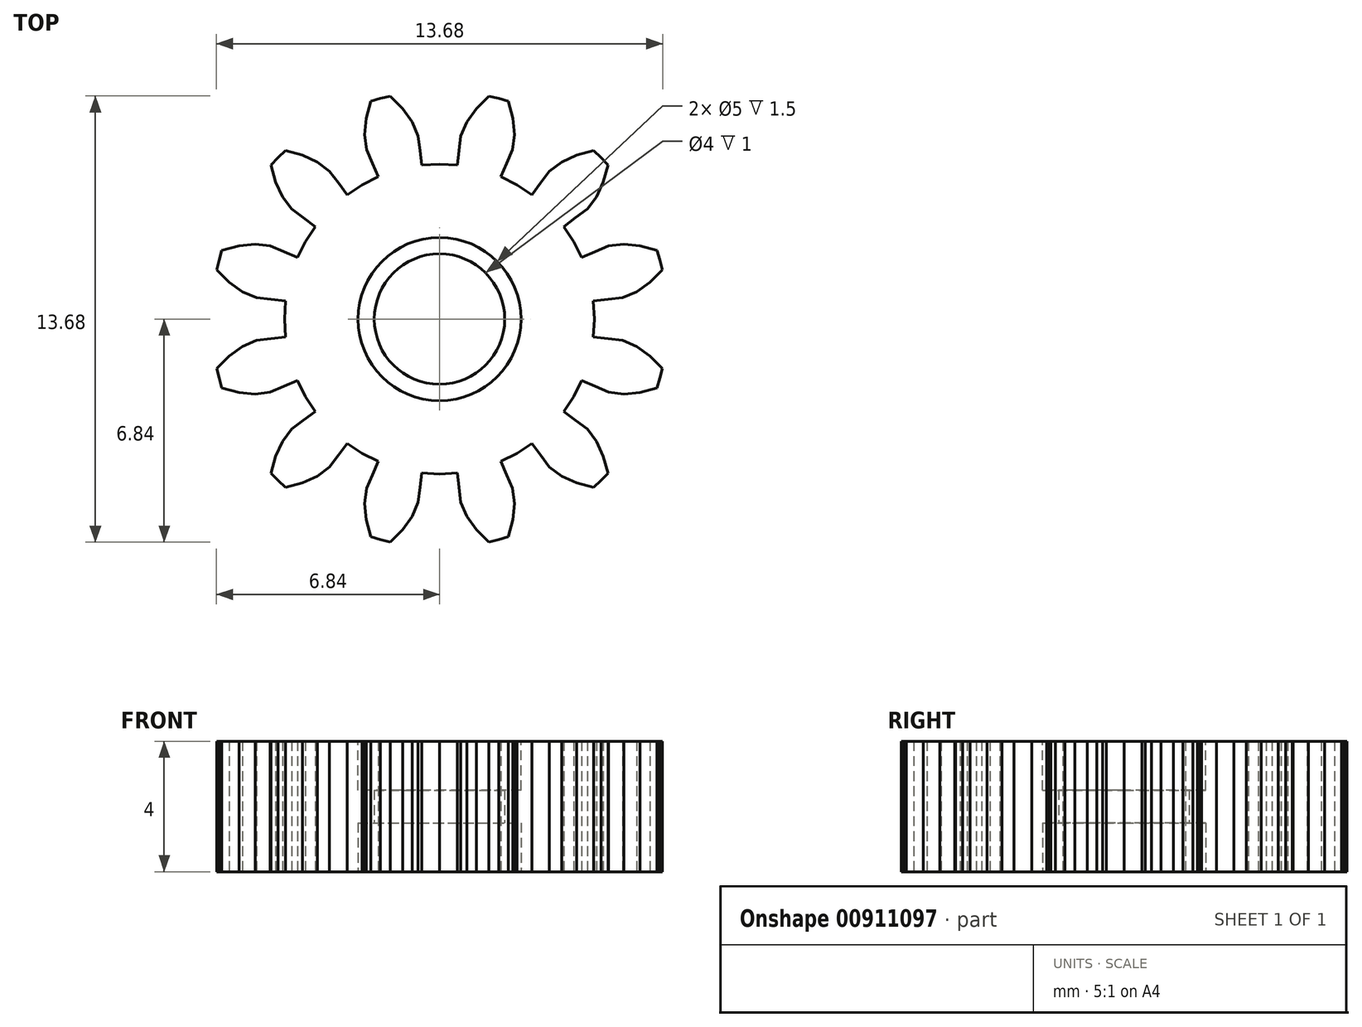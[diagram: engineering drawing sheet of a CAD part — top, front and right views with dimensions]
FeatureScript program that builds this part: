
annotation { "Feature Type Name" : "Feature", "Feature Type Description" : "" }
export const myFeature = defineFeature(function(context is Context, id is Id, definition is map)
    precondition{}
    {
        {
            var Q0;
            Q0=qCreatedBy(makeId("Top.planeOp"),FACE);
            var sketch = newSketch(context, id + "F0", { "sketchPlane" : qUnion([Q0])});
            skLineSegment(sketch, "E0", {"start": v(4.75, 0) * mm, "end": v(4.72, 0.55) * mm});
            skLineSegment(sketch, "E1", {"start": v(4.72, 0.55) * mm, "end": v(5.17, 0.6) * mm});
            skLineSegment(sketch, "E2", {"start": v(5.17, 0.6) * mm, "end": v(5.61, 0.65) * mm});
            skLineSegment(sketch, "E3", {"start": v(5.61, 0.65) * mm, "end": v(6.04, 0.84) * mm});
            skLineSegment(sketch, "E4", {"start": v(6.04, 0.84) * mm, "end": v(6.45, 1.13) * mm});
            skLineSegment(sketch, "E5", {"start": v(6.45, 1.13) * mm, "end": v(6.84, 1.51) * mm});
            skLineSegment(sketch, "E6", {"start": v(6.84, 1.51) * mm, "end": v(6.76, 1.81) * mm});
            skLineSegment(sketch, "E7", {"start": v(6.76, 1.81) * mm, "end": v(6.67, 2.1) * mm});
            skLineSegment(sketch, "E8", {"start": v(6.67, 2.1) * mm, "end": v(6.15, 2.25) * mm});
            skLineSegment(sketch, "E9", {"start": v(6.15, 2.25) * mm, "end": v(5.65, 2.3) * mm});
            skLineSegment(sketch, "E10", {"start": v(5.65, 2.3) * mm, "end": v(5.19, 2.24) * mm});
            skLineSegment(sketch, "E11", {"start": v(5.19, 2.24) * mm, "end": v(4.77, 2.06) * mm});
            skLineSegment(sketch, "E12", {"start": v(4.77, 2.06) * mm, "end": v(4.36, 1.88) * mm});
            skLineSegment(sketch, "E13", {"start": v(4.36, 1.88) * mm, "end": v(4.11, 2.38) * mm});
            skLineSegment(sketch, "E14", {"start": v(4.11, 2.38) * mm, "end": v(3.81, 2.84) * mm});
            skLineSegment(sketch, "E15", {"start": v(3.81, 2.84) * mm, "end": v(4.17, 3.1) * mm});
            skLineSegment(sketch, "E16", {"start": v(4.17, 3.1) * mm, "end": v(4.53, 3.37) * mm});
            skLineSegment(sketch, "E17", {"start": v(4.53, 3.37) * mm, "end": v(4.82, 3.74) * mm});
            skLineSegment(sketch, "E18", {"start": v(4.82, 3.74) * mm, "end": v(5.02, 4.2) * mm});
            skLineSegment(sketch, "E19", {"start": v(5.02, 4.2) * mm, "end": v(5.16, 4.73) * mm});
            skLineSegment(sketch, "E20", {"start": v(5.16, 4.73) * mm, "end": v(4.95, 4.95) * mm});
            skLineSegment(sketch, "E21", {"start": v(4.95, 4.95) * mm, "end": v(4.73, 5.16) * mm});
            skLineSegment(sketch, "E22", {"start": v(4.73, 5.16) * mm, "end": v(4.2, 5.02) * mm});
            skLineSegment(sketch, "E23", {"start": v(4.2, 5.02) * mm, "end": v(3.74, 4.82) * mm});
            skLineSegment(sketch, "E24", {"start": v(3.74, 4.82) * mm, "end": v(3.37, 4.53) * mm});
            skLineSegment(sketch, "E25", {"start": v(3.37, 4.53) * mm, "end": v(3.1, 4.17) * mm});
            skLineSegment(sketch, "E26", {"start": v(3.1, 4.17) * mm, "end": v(2.84, 3.81) * mm});
            skLineSegment(sketch, "E27", {"start": v(2.84, 3.81) * mm, "end": v(2.38, 4.11) * mm});
            skLineSegment(sketch, "E28", {"start": v(2.38, 4.11) * mm, "end": v(1.88, 4.36) * mm});
            skLineSegment(sketch, "E29", {"start": v(1.88, 4.36) * mm, "end": v(2.06, 4.77) * mm});
            skLineSegment(sketch, "E30", {"start": v(2.06, 4.77) * mm, "end": v(2.24, 5.19) * mm});
            skLineSegment(sketch, "E31", {"start": v(2.24, 5.19) * mm, "end": v(2.3, 5.65) * mm});
            skLineSegment(sketch, "E32", {"start": v(2.3, 5.65) * mm, "end": v(2.25, 6.15) * mm});
            skLineSegment(sketch, "E33", {"start": v(2.25, 6.15) * mm, "end": v(2.1, 6.67) * mm});
            skLineSegment(sketch, "E34", {"start": v(2.1, 6.67) * mm, "end": v(1.81, 6.76) * mm});
            skLineSegment(sketch, "E35", {"start": v(1.81, 6.76) * mm, "end": v(1.51, 6.84) * mm});
            skLineSegment(sketch, "E36", {"start": v(1.51, 6.84) * mm, "end": v(1.13, 6.45) * mm});
            skLineSegment(sketch, "E37", {"start": v(1.13, 6.45) * mm, "end": v(0.84, 6.04) * mm});
            skLineSegment(sketch, "E38", {"start": v(0.84, 6.04) * mm, "end": v(0.65, 5.61) * mm});
            skLineSegment(sketch, "E39", {"start": v(0.65, 5.61) * mm, "end": v(0.6, 5.17) * mm});
            skLineSegment(sketch, "E40", {"start": v(0.6, 5.17) * mm, "end": v(0.55, 4.72) * mm});
            skLineSegment(sketch, "E41", {"start": v(0.55, 4.72) * mm, "end": v(0, 4.75) * mm});
            skLineSegment(sketch, "E42", {"start": v(0, 4.75) * mm, "end": v(-0.55, 4.72) * mm});
            skLineSegment(sketch, "E43", {"start": v(-0.55, 4.72) * mm, "end": v(-0.6, 5.17) * mm});
            skLineSegment(sketch, "E44", {"start": v(-0.6, 5.17) * mm, "end": v(-0.65, 5.61) * mm});
            skLineSegment(sketch, "E45", {"start": v(-0.65, 5.61) * mm, "end": v(-0.84, 6.04) * mm});
            skLineSegment(sketch, "E46", {"start": v(-0.84, 6.04) * mm, "end": v(-1.13, 6.45) * mm});
            skLineSegment(sketch, "E47", {"start": v(-1.13, 6.45) * mm, "end": v(-1.51, 6.84) * mm});
            skLineSegment(sketch, "E48", {"start": v(-1.51, 6.84) * mm, "end": v(-1.81, 6.76) * mm});
            skLineSegment(sketch, "E49", {"start": v(-1.81, 6.76) * mm, "end": v(-2.1, 6.67) * mm});
            skLineSegment(sketch, "E50", {"start": v(-2.1, 6.67) * mm, "end": v(-2.25, 6.15) * mm});
            skLineSegment(sketch, "E51", {"start": v(-2.25, 6.15) * mm, "end": v(-2.3, 5.65) * mm});
            skLineSegment(sketch, "E52", {"start": v(-2.3, 5.65) * mm, "end": v(-2.24, 5.19) * mm});
            skLineSegment(sketch, "E53", {"start": v(-2.24, 5.19) * mm, "end": v(-2.06, 4.77) * mm});
            skLineSegment(sketch, "E54", {"start": v(-2.06, 4.77) * mm, "end": v(-1.88, 4.36) * mm});
            skLineSegment(sketch, "E55", {"start": v(-1.88, 4.36) * mm, "end": v(-2.38, 4.11) * mm});
            skLineSegment(sketch, "E56", {"start": v(-2.38, 4.11) * mm, "end": v(-2.84, 3.81) * mm});
            skLineSegment(sketch, "E57", {"start": v(-2.84, 3.81) * mm, "end": v(-3.1, 4.17) * mm});
            skLineSegment(sketch, "E58", {"start": v(-3.1, 4.17) * mm, "end": v(-3.37, 4.53) * mm});
            skLineSegment(sketch, "E59", {"start": v(-3.37, 4.53) * mm, "end": v(-3.74, 4.82) * mm});
            skLineSegment(sketch, "E60", {"start": v(-3.74, 4.82) * mm, "end": v(-4.2, 5.02) * mm});
            skLineSegment(sketch, "E61", {"start": v(-4.2, 5.02) * mm, "end": v(-4.73, 5.16) * mm});
            skLineSegment(sketch, "E62", {"start": v(-4.73, 5.16) * mm, "end": v(-4.95, 4.95) * mm});
            skLineSegment(sketch, "E63", {"start": v(-4.95, 4.95) * mm, "end": v(-5.16, 4.73) * mm});
            skLineSegment(sketch, "E64", {"start": v(-5.16, 4.73) * mm, "end": v(-5.02, 4.2) * mm});
            skLineSegment(sketch, "E65", {"start": v(-5.02, 4.2) * mm, "end": v(-4.82, 3.74) * mm});
            skLineSegment(sketch, "E66", {"start": v(-4.82, 3.74) * mm, "end": v(-4.53, 3.37) * mm});
            skLineSegment(sketch, "E67", {"start": v(-4.53, 3.37) * mm, "end": v(-4.17, 3.1) * mm});
            skLineSegment(sketch, "E68", {"start": v(-4.17, 3.1) * mm, "end": v(-3.81, 2.84) * mm});
            skLineSegment(sketch, "E69", {"start": v(-3.81, 2.84) * mm, "end": v(-4.11, 2.38) * mm});
            skLineSegment(sketch, "E70", {"start": v(-4.11, 2.38) * mm, "end": v(-4.36, 1.88) * mm});
            skLineSegment(sketch, "E71", {"start": v(-4.36, 1.88) * mm, "end": v(-4.77, 2.06) * mm});
            skLineSegment(sketch, "E72", {"start": v(-4.77, 2.06) * mm, "end": v(-5.19, 2.24) * mm});
            skLineSegment(sketch, "E73", {"start": v(-5.19, 2.24) * mm, "end": v(-5.65, 2.3) * mm});
            skLineSegment(sketch, "E74", {"start": v(-5.65, 2.3) * mm, "end": v(-6.15, 2.25) * mm});
            skLineSegment(sketch, "E75", {"start": v(-6.15, 2.25) * mm, "end": v(-6.67, 2.1) * mm});
            skLineSegment(sketch, "E76", {"start": v(-6.67, 2.1) * mm, "end": v(-6.76, 1.81) * mm});
            skLineSegment(sketch, "E77", {"start": v(-6.76, 1.81) * mm, "end": v(-6.84, 1.51) * mm});
            skLineSegment(sketch, "E78", {"start": v(-6.84, 1.51) * mm, "end": v(-6.45, 1.13) * mm});
            skLineSegment(sketch, "E79", {"start": v(-6.45, 1.13) * mm, "end": v(-6.04, 0.84) * mm});
            skLineSegment(sketch, "E80", {"start": v(-6.04, 0.84) * mm, "end": v(-5.61, 0.65) * mm});
            skLineSegment(sketch, "E81", {"start": v(-5.61, 0.65) * mm, "end": v(-5.17, 0.6) * mm});
            skLineSegment(sketch, "E82", {"start": v(-5.17, 0.6) * mm, "end": v(-4.72, 0.55) * mm});
            skLineSegment(sketch, "E83", {"start": v(-4.72, 0.55) * mm, "end": v(-4.75, 0) * mm});
            skLineSegment(sketch, "E84", {"start": v(-4.75, 0) * mm, "end": v(-4.72, -0.55) * mm});
            skLineSegment(sketch, "E85", {"start": v(-4.72, -0.55) * mm, "end": v(-5.17, -0.6) * mm});
            skLineSegment(sketch, "E86", {"start": v(-5.17, -0.6) * mm, "end": v(-5.61, -0.65) * mm});
            skLineSegment(sketch, "E87", {"start": v(-5.61, -0.65) * mm, "end": v(-6.04, -0.84) * mm});
            skLineSegment(sketch, "E88", {"start": v(-6.04, -0.84) * mm, "end": v(-6.45, -1.13) * mm});
            skLineSegment(sketch, "E89", {"start": v(-6.45, -1.13) * mm, "end": v(-6.84, -1.51) * mm});
            skLineSegment(sketch, "E90", {"start": v(-6.84, -1.51) * mm, "end": v(-6.76, -1.81) * mm});
            skLineSegment(sketch, "E91", {"start": v(-6.76, -1.81) * mm, "end": v(-6.67, -2.1) * mm});
            skLineSegment(sketch, "E92", {"start": v(-6.67, -2.1) * mm, "end": v(-6.15, -2.25) * mm});
            skLineSegment(sketch, "E93", {"start": v(-6.15, -2.25) * mm, "end": v(-5.65, -2.3) * mm});
            skLineSegment(sketch, "E94", {"start": v(-5.65, -2.3) * mm, "end": v(-5.19, -2.24) * mm});
            skLineSegment(sketch, "E95", {"start": v(-5.19, -2.24) * mm, "end": v(-4.77, -2.06) * mm});
            skLineSegment(sketch, "E96", {"start": v(-4.77, -2.06) * mm, "end": v(-4.36, -1.88) * mm});
            skLineSegment(sketch, "E97", {"start": v(-4.36, -1.88) * mm, "end": v(-4.11, -2.38) * mm});
            skLineSegment(sketch, "E98", {"start": v(-4.11, -2.38) * mm, "end": v(-3.81, -2.84) * mm});
            skLineSegment(sketch, "E99", {"start": v(-3.81, -2.84) * mm, "end": v(-4.17, -3.1) * mm});
            skLineSegment(sketch, "E100", {"start": v(-4.17, -3.1) * mm, "end": v(-4.53, -3.37) * mm});
            skLineSegment(sketch, "E101", {"start": v(-4.53, -3.37) * mm, "end": v(-4.82, -3.74) * mm});
            skLineSegment(sketch, "E102", {"start": v(-4.82, -3.74) * mm, "end": v(-5.02, -4.2) * mm});
            skLineSegment(sketch, "E103", {"start": v(-5.02, -4.2) * mm, "end": v(-5.16, -4.73) * mm});
            skLineSegment(sketch, "E104", {"start": v(-5.16, -4.73) * mm, "end": v(-4.95, -4.95) * mm});
            skLineSegment(sketch, "E105", {"start": v(-4.95, -4.95) * mm, "end": v(-4.73, -5.16) * mm});
            skLineSegment(sketch, "E106", {"start": v(-4.73, -5.16) * mm, "end": v(-4.2, -5.02) * mm});
            skLineSegment(sketch, "E107", {"start": v(-4.2, -5.02) * mm, "end": v(-3.74, -4.82) * mm});
            skLineSegment(sketch, "E108", {"start": v(-3.74, -4.82) * mm, "end": v(-3.37, -4.53) * mm});
            skLineSegment(sketch, "E109", {"start": v(-3.37, -4.53) * mm, "end": v(-3.1, -4.17) * mm});
            skLineSegment(sketch, "E110", {"start": v(-3.1, -4.17) * mm, "end": v(-2.84, -3.81) * mm});
            skLineSegment(sketch, "E111", {"start": v(-2.84, -3.81) * mm, "end": v(-2.38, -4.11) * mm});
            skLineSegment(sketch, "E112", {"start": v(-2.38, -4.11) * mm, "end": v(-1.88, -4.36) * mm});
            skLineSegment(sketch, "E113", {"start": v(-1.88, -4.36) * mm, "end": v(-2.06, -4.77) * mm});
            skLineSegment(sketch, "E114", {"start": v(-2.06, -4.77) * mm, "end": v(-2.24, -5.19) * mm});
            skLineSegment(sketch, "E115", {"start": v(-2.24, -5.19) * mm, "end": v(-2.3, -5.65) * mm});
            skLineSegment(sketch, "E116", {"start": v(-2.3, -5.65) * mm, "end": v(-2.25, -6.15) * mm});
            skLineSegment(sketch, "E117", {"start": v(-2.25, -6.15) * mm, "end": v(-2.1, -6.67) * mm});
            skLineSegment(sketch, "E118", {"start": v(-2.1, -6.67) * mm, "end": v(-1.81, -6.76) * mm});
            skLineSegment(sketch, "E119", {"start": v(-1.81, -6.76) * mm, "end": v(-1.51, -6.84) * mm});
            skLineSegment(sketch, "E120", {"start": v(-1.51, -6.84) * mm, "end": v(-1.13, -6.45) * mm});
            skLineSegment(sketch, "E121", {"start": v(-1.13, -6.45) * mm, "end": v(-0.84, -6.04) * mm});
            skLineSegment(sketch, "E122", {"start": v(-0.84, -6.04) * mm, "end": v(-0.65, -5.61) * mm});
            skLineSegment(sketch, "E123", {"start": v(-0.65, -5.61) * mm, "end": v(-0.6, -5.17) * mm});
            skLineSegment(sketch, "E124", {"start": v(-0.6, -5.17) * mm, "end": v(-0.55, -4.72) * mm});
            skLineSegment(sketch, "E125", {"start": v(-0.55, -4.72) * mm, "end": v(0, -4.75) * mm});
            skLineSegment(sketch, "E126", {"start": v(0, -4.75) * mm, "end": v(0.55, -4.72) * mm});
            skLineSegment(sketch, "E127", {"start": v(0.55, -4.72) * mm, "end": v(0.6, -5.17) * mm});
            skLineSegment(sketch, "E128", {"start": v(0.6, -5.17) * mm, "end": v(0.65, -5.61) * mm});
            skLineSegment(sketch, "E129", {"start": v(0.65, -5.61) * mm, "end": v(0.84, -6.04) * mm});
            skLineSegment(sketch, "E130", {"start": v(0.84, -6.04) * mm, "end": v(1.13, -6.45) * mm});
            skLineSegment(sketch, "E131", {"start": v(1.13, -6.45) * mm, "end": v(1.51, -6.84) * mm});
            skLineSegment(sketch, "E132", {"start": v(1.51, -6.84) * mm, "end": v(1.81, -6.76) * mm});
            skLineSegment(sketch, "E133", {"start": v(1.81, -6.76) * mm, "end": v(2.1, -6.67) * mm});
            skLineSegment(sketch, "E134", {"start": v(2.1, -6.67) * mm, "end": v(2.25, -6.15) * mm});
            skLineSegment(sketch, "E135", {"start": v(2.25, -6.15) * mm, "end": v(2.3, -5.65) * mm});
            skLineSegment(sketch, "E136", {"start": v(2.3, -5.65) * mm, "end": v(2.24, -5.19) * mm});
            skLineSegment(sketch, "E137", {"start": v(2.24, -5.19) * mm, "end": v(2.06, -4.77) * mm});
            skLineSegment(sketch, "E138", {"start": v(2.06, -4.77) * mm, "end": v(1.88, -4.36) * mm});
            skLineSegment(sketch, "E139", {"start": v(1.88, -4.36) * mm, "end": v(2.38, -4.11) * mm});
            skLineSegment(sketch, "E140", {"start": v(2.38, -4.11) * mm, "end": v(2.84, -3.81) * mm});
            skLineSegment(sketch, "E141", {"start": v(2.84, -3.81) * mm, "end": v(3.1, -4.17) * mm});
            skLineSegment(sketch, "E142", {"start": v(3.1, -4.17) * mm, "end": v(3.37, -4.53) * mm});
            skLineSegment(sketch, "E143", {"start": v(3.37, -4.53) * mm, "end": v(3.74, -4.82) * mm});
            skLineSegment(sketch, "E144", {"start": v(3.74, -4.82) * mm, "end": v(4.2, -5.02) * mm});
            skLineSegment(sketch, "E145", {"start": v(4.2, -5.02) * mm, "end": v(4.73, -5.16) * mm});
            skLineSegment(sketch, "E146", {"start": v(4.73, -5.16) * mm, "end": v(4.95, -4.95) * mm});
            skLineSegment(sketch, "E147", {"start": v(4.95, -4.95) * mm, "end": v(5.16, -4.73) * mm});
            skLineSegment(sketch, "E148", {"start": v(5.16, -4.73) * mm, "end": v(5.02, -4.2) * mm});
            skLineSegment(sketch, "E149", {"start": v(5.02, -4.2) * mm, "end": v(4.82, -3.74) * mm});
            skLineSegment(sketch, "E150", {"start": v(4.82, -3.74) * mm, "end": v(4.53, -3.37) * mm});
            skLineSegment(sketch, "E151", {"start": v(4.53, -3.37) * mm, "end": v(4.17, -3.1) * mm});
            skLineSegment(sketch, "E152", {"start": v(4.17, -3.1) * mm, "end": v(3.81, -2.84) * mm});
            skLineSegment(sketch, "E153", {"start": v(3.81, -2.84) * mm, "end": v(4.11, -2.38) * mm});
            skLineSegment(sketch, "E154", {"start": v(4.11, -2.38) * mm, "end": v(4.36, -1.88) * mm});
            skLineSegment(sketch, "E155", {"start": v(4.36, -1.88) * mm, "end": v(4.77, -2.06) * mm});
            skLineSegment(sketch, "E156", {"start": v(4.77, -2.06) * mm, "end": v(5.19, -2.24) * mm});
            skLineSegment(sketch, "E157", {"start": v(5.19, -2.24) * mm, "end": v(5.65, -2.3) * mm});
            skLineSegment(sketch, "E158", {"start": v(5.65, -2.3) * mm, "end": v(6.15, -2.25) * mm});
            skLineSegment(sketch, "E159", {"start": v(6.15, -2.25) * mm, "end": v(6.67, -2.1) * mm});
            skLineSegment(sketch, "E160", {"start": v(6.67, -2.1) * mm, "end": v(6.76, -1.81) * mm});
            skLineSegment(sketch, "E161", {"start": v(6.76, -1.81) * mm, "end": v(6.84, -1.51) * mm});
            skLineSegment(sketch, "E162", {"start": v(6.84, -1.51) * mm, "end": v(6.45, -1.13) * mm});
            skLineSegment(sketch, "E163", {"start": v(6.45, -1.13) * mm, "end": v(6.04, -0.84) * mm});
            skLineSegment(sketch, "E164", {"start": v(6.04, -0.84) * mm, "end": v(5.61, -0.65) * mm});
            skLineSegment(sketch, "E165", {"start": v(5.61, -0.65) * mm, "end": v(5.17, -0.6) * mm});
            skLineSegment(sketch, "E166", {"start": v(5.17, -0.6) * mm, "end": v(4.72, -0.55) * mm});
            skLineSegment(sketch, "E167", {"start": v(4.75, 0) * mm, "end": v(4.72, -0.55) * mm});
            skCircle(sketch, "E168", {"center": v(0, 0) * mm, "radius": 7 * mm, "construction": true});
            skCircle(sketch, "E169", {"center": v(0, 0) * mm, "radius": 2 * mm});
            skSolve(sketch);
        }
        {
            var Q0;
            Q0 = qSketchRegion(id + "F0", true);
            extrude(context, id + "F1", {"entities" : qUnion([Q0]), "depth" : 4 * mm, "offsetDistance" : 25 * mm});
        }
        {
            var Q0;
            Q0=makeQuery(id+"F1.opExtrude","CAP_FACE",FACE,{"disambiguationData":[OSD([sQuery(id+"F0.wireOp",EDGE,"E0"),sQuery(id+"F0.wireOp",EDGE,"E1"),sQuery(id+"F0.wireOp",EDGE,"E2"),sQuery(id+"F0.wireOp",EDGE,"E3"),sQuery(id+"F0.wireOp",EDGE,"E4"),sQuery(id+"F0.wireOp",EDGE,"E5"),sQuery(id+"F0.wireOp",EDGE,"E6"),sQuery(id+"F0.wireOp",EDGE,"E7"),sQuery(id+"F0.wireOp",EDGE,"E8"),sQuery(id+"F0.wireOp",EDGE,"E9"),sQuery(id+"F0.wireOp",EDGE,"E10"),sQuery(id+"F0.wireOp",EDGE,"E11"),sQuery(id+"F0.wireOp",EDGE,"E12"),sQuery(id+"F0.wireOp",EDGE,"E13"),sQuery(id+"F0.wireOp",EDGE,"E14"),sQuery(id+"F0.wireOp",EDGE,"E15"),sQuery(id+"F0.wireOp",EDGE,"E16"),sQuery(id+"F0.wireOp",EDGE,"E17"),sQuery(id+"F0.wireOp",EDGE,"E18"),sQuery(id+"F0.wireOp",EDGE,"E19"),sQuery(id+"F0.wireOp",EDGE,"E20"),sQuery(id+"F0.wireOp",EDGE,"E21"),sQuery(id+"F0.wireOp",EDGE,"E22"),sQuery(id+"F0.wireOp",EDGE,"E23"),sQuery(id+"F0.wireOp",EDGE,"E24"),sQuery(id+"F0.wireOp",EDGE,"E25"),sQuery(id+"F0.wireOp",EDGE,"E26"),sQuery(id+"F0.wireOp",EDGE,"E27"),sQuery(id+"F0.wireOp",EDGE,"E28"),sQuery(id+"F0.wireOp",EDGE,"E29"),sQuery(id+"F0.wireOp",EDGE,"E30"),sQuery(id+"F0.wireOp",EDGE,"E31"),sQuery(id+"F0.wireOp",EDGE,"E32"),sQuery(id+"F0.wireOp",EDGE,"E33"),sQuery(id+"F0.wireOp",EDGE,"E34"),sQuery(id+"F0.wireOp",EDGE,"E35"),sQuery(id+"F0.wireOp",EDGE,"E36"),sQuery(id+"F0.wireOp",EDGE,"E37"),sQuery(id+"F0.wireOp",EDGE,"E38"),sQuery(id+"F0.wireOp",EDGE,"E39"),sQuery(id+"F0.wireOp",EDGE,"E40"),sQuery(id+"F0.wireOp",EDGE,"E41"),sQuery(id+"F0.wireOp",EDGE,"E42"),sQuery(id+"F0.wireOp",EDGE,"E43"),sQuery(id+"F0.wireOp",EDGE,"E44"),sQuery(id+"F0.wireOp",EDGE,"E45"),sQuery(id+"F0.wireOp",EDGE,"E46"),sQuery(id+"F0.wireOp",EDGE,"E47"),sQuery(id+"F0.wireOp",EDGE,"E48"),sQuery(id+"F0.wireOp",EDGE,"E49"),sQuery(id+"F0.wireOp",EDGE,"E50"),sQuery(id+"F0.wireOp",EDGE,"E51"),sQuery(id+"F0.wireOp",EDGE,"E52"),sQuery(id+"F0.wireOp",EDGE,"E53"),sQuery(id+"F0.wireOp",EDGE,"E54"),sQuery(id+"F0.wireOp",EDGE,"E55"),sQuery(id+"F0.wireOp",EDGE,"E56"),sQuery(id+"F0.wireOp",EDGE,"E57"),sQuery(id+"F0.wireOp",EDGE,"E58"),sQuery(id+"F0.wireOp",EDGE,"E59"),sQuery(id+"F0.wireOp",EDGE,"E60"),sQuery(id+"F0.wireOp",EDGE,"E61"),sQuery(id+"F0.wireOp",EDGE,"E62"),sQuery(id+"F0.wireOp",EDGE,"E63"),sQuery(id+"F0.wireOp",EDGE,"E64"),sQuery(id+"F0.wireOp",EDGE,"E65"),sQuery(id+"F0.wireOp",EDGE,"E66"),sQuery(id+"F0.wireOp",EDGE,"E67"),sQuery(id+"F0.wireOp",EDGE,"E68"),sQuery(id+"F0.wireOp",EDGE,"E69"),sQuery(id+"F0.wireOp",EDGE,"E70"),sQuery(id+"F0.wireOp",EDGE,"E71"),sQuery(id+"F0.wireOp",EDGE,"E72"),sQuery(id+"F0.wireOp",EDGE,"E73"),sQuery(id+"F0.wireOp",EDGE,"E74"),sQuery(id+"F0.wireOp",EDGE,"E75"),sQuery(id+"F0.wireOp",EDGE,"E76"),sQuery(id+"F0.wireOp",EDGE,"E77"),sQuery(id+"F0.wireOp",EDGE,"E78"),sQuery(id+"F0.wireOp",EDGE,"E79"),sQuery(id+"F0.wireOp",EDGE,"E80"),sQuery(id+"F0.wireOp",EDGE,"E81"),sQuery(id+"F0.wireOp",EDGE,"E82"),sQuery(id+"F0.wireOp",EDGE,"E83"),sQuery(id+"F0.wireOp",EDGE,"E84"),sQuery(id+"F0.wireOp",EDGE,"E85"),sQuery(id+"F0.wireOp",EDGE,"E86"),sQuery(id+"F0.wireOp",EDGE,"E87"),sQuery(id+"F0.wireOp",EDGE,"E88"),sQuery(id+"F0.wireOp",EDGE,"E89"),sQuery(id+"F0.wireOp",EDGE,"E90"),sQuery(id+"F0.wireOp",EDGE,"E91"),sQuery(id+"F0.wireOp",EDGE,"E92"),sQuery(id+"F0.wireOp",EDGE,"E93"),sQuery(id+"F0.wireOp",EDGE,"E94"),sQuery(id+"F0.wireOp",EDGE,"E95"),sQuery(id+"F0.wireOp",EDGE,"E96"),sQuery(id+"F0.wireOp",EDGE,"E97"),sQuery(id+"F0.wireOp",EDGE,"E98"),sQuery(id+"F0.wireOp",EDGE,"E99"),sQuery(id+"F0.wireOp",EDGE,"E100"),sQuery(id+"F0.wireOp",EDGE,"E101"),sQuery(id+"F0.wireOp",EDGE,"E102"),sQuery(id+"F0.wireOp",EDGE,"E103"),sQuery(id+"F0.wireOp",EDGE,"E104"),sQuery(id+"F0.wireOp",EDGE,"E105"),sQuery(id+"F0.wireOp",EDGE,"E106"),sQuery(id+"F0.wireOp",EDGE,"E107"),sQuery(id+"F0.wireOp",EDGE,"E108"),sQuery(id+"F0.wireOp",EDGE,"E109"),sQuery(id+"F0.wireOp",EDGE,"E110"),sQuery(id+"F0.wireOp",EDGE,"E111"),sQuery(id+"F0.wireOp",EDGE,"E112"),sQuery(id+"F0.wireOp",EDGE,"E113"),sQuery(id+"F0.wireOp",EDGE,"E114"),sQuery(id+"F0.wireOp",EDGE,"E115"),sQuery(id+"F0.wireOp",EDGE,"E116"),sQuery(id+"F0.wireOp",EDGE,"E117"),sQuery(id+"F0.wireOp",EDGE,"E118"),sQuery(id+"F0.wireOp",EDGE,"E119"),sQuery(id+"F0.wireOp",EDGE,"E120"),sQuery(id+"F0.wireOp",EDGE,"E121"),sQuery(id+"F0.wireOp",EDGE,"E122"),sQuery(id+"F0.wireOp",EDGE,"E123"),sQuery(id+"F0.wireOp",EDGE,"E124"),sQuery(id+"F0.wireOp",EDGE,"E125"),sQuery(id+"F0.wireOp",EDGE,"E126"),sQuery(id+"F0.wireOp",EDGE,"E127"),sQuery(id+"F0.wireOp",EDGE,"E128"),sQuery(id+"F0.wireOp",EDGE,"E129"),sQuery(id+"F0.wireOp",EDGE,"E130"),sQuery(id+"F0.wireOp",EDGE,"E131"),sQuery(id+"F0.wireOp",EDGE,"E132"),sQuery(id+"F0.wireOp",EDGE,"E133"),sQuery(id+"F0.wireOp",EDGE,"E134"),sQuery(id+"F0.wireOp",EDGE,"E135"),sQuery(id+"F0.wireOp",EDGE,"E136"),sQuery(id+"F0.wireOp",EDGE,"E137"),sQuery(id+"F0.wireOp",EDGE,"E138"),sQuery(id+"F0.wireOp",EDGE,"E139"),sQuery(id+"F0.wireOp",EDGE,"E140"),sQuery(id+"F0.wireOp",EDGE,"E141"),sQuery(id+"F0.wireOp",EDGE,"E142"),sQuery(id+"F0.wireOp",EDGE,"E143"),sQuery(id+"F0.wireOp",EDGE,"E144"),sQuery(id+"F0.wireOp",EDGE,"E145"),sQuery(id+"F0.wireOp",EDGE,"E146"),sQuery(id+"F0.wireOp",EDGE,"E147"),sQuery(id+"F0.wireOp",EDGE,"E148"),sQuery(id+"F0.wireOp",EDGE,"E149"),sQuery(id+"F0.wireOp",EDGE,"E150"),sQuery(id+"F0.wireOp",EDGE,"E151"),sQuery(id+"F0.wireOp",EDGE,"E152"),sQuery(id+"F0.wireOp",EDGE,"E153"),sQuery(id+"F0.wireOp",EDGE,"E154"),sQuery(id+"F0.wireOp",EDGE,"E155"),sQuery(id+"F0.wireOp",EDGE,"E156"),sQuery(id+"F0.wireOp",EDGE,"E157"),sQuery(id+"F0.wireOp",EDGE,"E158"),sQuery(id+"F0.wireOp",EDGE,"E159"),sQuery(id+"F0.wireOp",EDGE,"E160"),sQuery(id+"F0.wireOp",EDGE,"E161"),sQuery(id+"F0.wireOp",EDGE,"E162"),sQuery(id+"F0.wireOp",EDGE,"E163"),sQuery(id+"F0.wireOp",EDGE,"E164"),sQuery(id+"F0.wireOp",EDGE,"E165"),sQuery(id+"F0.wireOp",EDGE,"E166"),sQuery(id+"F0.wireOp",EDGE,"E167"),sQuery(id+"F0.wireOp",EDGE,"E169")])],"isStart":false});
            var sketch = newSketch(context, id + "F2", { "sketchPlane" : qUnion([Q0])});
            skCircle(sketch, "E170", {"center": v(0, 0) * mm, "radius": 2 * mm, "construction": true});
            skPoint(sketch, "E170.first.point", {"position": v(-1.69, 1.07) * mm});
            skPoint(sketch, "E170.second.point", {"position": v(-0.57, 1.92) * mm});
            skPoint(sketch, "E170.third.point", {"position": v(0.5, 1.94) * mm});
            skCircle(sketch, "E171", {"center": v(0, 0) * mm, "radius": 2.5 * mm});
            skSolve(sketch);
        }
        {
            var Q0;
            Q0 = qSketchRegion(id + "F2", true);
            extrude(context, id + "F3", {"entities" : qUnion([Q0]), "operationType" : NewBodyOperationType.REMOVE, "oppositeDirection" : true, "depth" : 1.5 * mm, "offsetDistance" : 25 * mm});
        }
        {
            var Q0;
            Q0=makeQuery(id+"F1.opExtrude","CAP_FACE",FACE,{"disambiguationData":[OSD([sQuery(id+"F0.wireOp",EDGE,"E0"),sQuery(id+"F0.wireOp",EDGE,"E1"),sQuery(id+"F0.wireOp",EDGE,"E2"),sQuery(id+"F0.wireOp",EDGE,"E3"),sQuery(id+"F0.wireOp",EDGE,"E4"),sQuery(id+"F0.wireOp",EDGE,"E5"),sQuery(id+"F0.wireOp",EDGE,"E6"),sQuery(id+"F0.wireOp",EDGE,"E7"),sQuery(id+"F0.wireOp",EDGE,"E8"),sQuery(id+"F0.wireOp",EDGE,"E9"),sQuery(id+"F0.wireOp",EDGE,"E10"),sQuery(id+"F0.wireOp",EDGE,"E11"),sQuery(id+"F0.wireOp",EDGE,"E12"),sQuery(id+"F0.wireOp",EDGE,"E13"),sQuery(id+"F0.wireOp",EDGE,"E14"),sQuery(id+"F0.wireOp",EDGE,"E15"),sQuery(id+"F0.wireOp",EDGE,"E16"),sQuery(id+"F0.wireOp",EDGE,"E17"),sQuery(id+"F0.wireOp",EDGE,"E18"),sQuery(id+"F0.wireOp",EDGE,"E19"),sQuery(id+"F0.wireOp",EDGE,"E20"),sQuery(id+"F0.wireOp",EDGE,"E21"),sQuery(id+"F0.wireOp",EDGE,"E22"),sQuery(id+"F0.wireOp",EDGE,"E23"),sQuery(id+"F0.wireOp",EDGE,"E24"),sQuery(id+"F0.wireOp",EDGE,"E25"),sQuery(id+"F0.wireOp",EDGE,"E26"),sQuery(id+"F0.wireOp",EDGE,"E27"),sQuery(id+"F0.wireOp",EDGE,"E28"),sQuery(id+"F0.wireOp",EDGE,"E29"),sQuery(id+"F0.wireOp",EDGE,"E30"),sQuery(id+"F0.wireOp",EDGE,"E31"),sQuery(id+"F0.wireOp",EDGE,"E32"),sQuery(id+"F0.wireOp",EDGE,"E33"),sQuery(id+"F0.wireOp",EDGE,"E34"),sQuery(id+"F0.wireOp",EDGE,"E35"),sQuery(id+"F0.wireOp",EDGE,"E36"),sQuery(id+"F0.wireOp",EDGE,"E37"),sQuery(id+"F0.wireOp",EDGE,"E38"),sQuery(id+"F0.wireOp",EDGE,"E39"),sQuery(id+"F0.wireOp",EDGE,"E40"),sQuery(id+"F0.wireOp",EDGE,"E41"),sQuery(id+"F0.wireOp",EDGE,"E42"),sQuery(id+"F0.wireOp",EDGE,"E43"),sQuery(id+"F0.wireOp",EDGE,"E44"),sQuery(id+"F0.wireOp",EDGE,"E45"),sQuery(id+"F0.wireOp",EDGE,"E46"),sQuery(id+"F0.wireOp",EDGE,"E47"),sQuery(id+"F0.wireOp",EDGE,"E48"),sQuery(id+"F0.wireOp",EDGE,"E49"),sQuery(id+"F0.wireOp",EDGE,"E50"),sQuery(id+"F0.wireOp",EDGE,"E51"),sQuery(id+"F0.wireOp",EDGE,"E52"),sQuery(id+"F0.wireOp",EDGE,"E53"),sQuery(id+"F0.wireOp",EDGE,"E54"),sQuery(id+"F0.wireOp",EDGE,"E55"),sQuery(id+"F0.wireOp",EDGE,"E56"),sQuery(id+"F0.wireOp",EDGE,"E57"),sQuery(id+"F0.wireOp",EDGE,"E58"),sQuery(id+"F0.wireOp",EDGE,"E59"),sQuery(id+"F0.wireOp",EDGE,"E60"),sQuery(id+"F0.wireOp",EDGE,"E61"),sQuery(id+"F0.wireOp",EDGE,"E62"),sQuery(id+"F0.wireOp",EDGE,"E63"),sQuery(id+"F0.wireOp",EDGE,"E64"),sQuery(id+"F0.wireOp",EDGE,"E65"),sQuery(id+"F0.wireOp",EDGE,"E66"),sQuery(id+"F0.wireOp",EDGE,"E67"),sQuery(id+"F0.wireOp",EDGE,"E68"),sQuery(id+"F0.wireOp",EDGE,"E69"),sQuery(id+"F0.wireOp",EDGE,"E70"),sQuery(id+"F0.wireOp",EDGE,"E71"),sQuery(id+"F0.wireOp",EDGE,"E72"),sQuery(id+"F0.wireOp",EDGE,"E73"),sQuery(id+"F0.wireOp",EDGE,"E74"),sQuery(id+"F0.wireOp",EDGE,"E75"),sQuery(id+"F0.wireOp",EDGE,"E76"),sQuery(id+"F0.wireOp",EDGE,"E77"),sQuery(id+"F0.wireOp",EDGE,"E78"),sQuery(id+"F0.wireOp",EDGE,"E79"),sQuery(id+"F0.wireOp",EDGE,"E80"),sQuery(id+"F0.wireOp",EDGE,"E81"),sQuery(id+"F0.wireOp",EDGE,"E82"),sQuery(id+"F0.wireOp",EDGE,"E83"),sQuery(id+"F0.wireOp",EDGE,"E84"),sQuery(id+"F0.wireOp",EDGE,"E85"),sQuery(id+"F0.wireOp",EDGE,"E86"),sQuery(id+"F0.wireOp",EDGE,"E87"),sQuery(id+"F0.wireOp",EDGE,"E88"),sQuery(id+"F0.wireOp",EDGE,"E89"),sQuery(id+"F0.wireOp",EDGE,"E90"),sQuery(id+"F0.wireOp",EDGE,"E91"),sQuery(id+"F0.wireOp",EDGE,"E92"),sQuery(id+"F0.wireOp",EDGE,"E93"),sQuery(id+"F0.wireOp",EDGE,"E94"),sQuery(id+"F0.wireOp",EDGE,"E95"),sQuery(id+"F0.wireOp",EDGE,"E96"),sQuery(id+"F0.wireOp",EDGE,"E97"),sQuery(id+"F0.wireOp",EDGE,"E98"),sQuery(id+"F0.wireOp",EDGE,"E99"),sQuery(id+"F0.wireOp",EDGE,"E100"),sQuery(id+"F0.wireOp",EDGE,"E101"),sQuery(id+"F0.wireOp",EDGE,"E102"),sQuery(id+"F0.wireOp",EDGE,"E103"),sQuery(id+"F0.wireOp",EDGE,"E104"),sQuery(id+"F0.wireOp",EDGE,"E105"),sQuery(id+"F0.wireOp",EDGE,"E106"),sQuery(id+"F0.wireOp",EDGE,"E107"),sQuery(id+"F0.wireOp",EDGE,"E108"),sQuery(id+"F0.wireOp",EDGE,"E109"),sQuery(id+"F0.wireOp",EDGE,"E110"),sQuery(id+"F0.wireOp",EDGE,"E111"),sQuery(id+"F0.wireOp",EDGE,"E112"),sQuery(id+"F0.wireOp",EDGE,"E113"),sQuery(id+"F0.wireOp",EDGE,"E114"),sQuery(id+"F0.wireOp",EDGE,"E115"),sQuery(id+"F0.wireOp",EDGE,"E116"),sQuery(id+"F0.wireOp",EDGE,"E117"),sQuery(id+"F0.wireOp",EDGE,"E118"),sQuery(id+"F0.wireOp",EDGE,"E119"),sQuery(id+"F0.wireOp",EDGE,"E120"),sQuery(id+"F0.wireOp",EDGE,"E121"),sQuery(id+"F0.wireOp",EDGE,"E122"),sQuery(id+"F0.wireOp",EDGE,"E123"),sQuery(id+"F0.wireOp",EDGE,"E124"),sQuery(id+"F0.wireOp",EDGE,"E125"),sQuery(id+"F0.wireOp",EDGE,"E126"),sQuery(id+"F0.wireOp",EDGE,"E127"),sQuery(id+"F0.wireOp",EDGE,"E128"),sQuery(id+"F0.wireOp",EDGE,"E129"),sQuery(id+"F0.wireOp",EDGE,"E130"),sQuery(id+"F0.wireOp",EDGE,"E131"),sQuery(id+"F0.wireOp",EDGE,"E132"),sQuery(id+"F0.wireOp",EDGE,"E133"),sQuery(id+"F0.wireOp",EDGE,"E134"),sQuery(id+"F0.wireOp",EDGE,"E135"),sQuery(id+"F0.wireOp",EDGE,"E136"),sQuery(id+"F0.wireOp",EDGE,"E137"),sQuery(id+"F0.wireOp",EDGE,"E138"),sQuery(id+"F0.wireOp",EDGE,"E139"),sQuery(id+"F0.wireOp",EDGE,"E140"),sQuery(id+"F0.wireOp",EDGE,"E141"),sQuery(id+"F0.wireOp",EDGE,"E142"),sQuery(id+"F0.wireOp",EDGE,"E143"),sQuery(id+"F0.wireOp",EDGE,"E144"),sQuery(id+"F0.wireOp",EDGE,"E145"),sQuery(id+"F0.wireOp",EDGE,"E146"),sQuery(id+"F0.wireOp",EDGE,"E147"),sQuery(id+"F0.wireOp",EDGE,"E148"),sQuery(id+"F0.wireOp",EDGE,"E149"),sQuery(id+"F0.wireOp",EDGE,"E150"),sQuery(id+"F0.wireOp",EDGE,"E151"),sQuery(id+"F0.wireOp",EDGE,"E152"),sQuery(id+"F0.wireOp",EDGE,"E153"),sQuery(id+"F0.wireOp",EDGE,"E154"),sQuery(id+"F0.wireOp",EDGE,"E155"),sQuery(id+"F0.wireOp",EDGE,"E156"),sQuery(id+"F0.wireOp",EDGE,"E157"),sQuery(id+"F0.wireOp",EDGE,"E158"),sQuery(id+"F0.wireOp",EDGE,"E159"),sQuery(id+"F0.wireOp",EDGE,"E160"),sQuery(id+"F0.wireOp",EDGE,"E161"),sQuery(id+"F0.wireOp",EDGE,"E162"),sQuery(id+"F0.wireOp",EDGE,"E163"),sQuery(id+"F0.wireOp",EDGE,"E164"),sQuery(id+"F0.wireOp",EDGE,"E165"),sQuery(id+"F0.wireOp",EDGE,"E166"),sQuery(id+"F0.wireOp",EDGE,"E167"),sQuery(id+"F0.wireOp",EDGE,"E169")])],"isStart":true});
            var sketch = newSketch(context, id + "F4", { "sketchPlane" : qUnion([Q0])});
            skCircle(sketch, "E172", {"center": v(0, 0) * mm, "radius": 2 * mm, "construction": true});
            skPoint(sketch, "E172.first.point", {"position": v(-1.79, -0.9) * mm});
            skPoint(sketch, "E172.second.point", {"position": v(-1.98, 0.25) * mm});
            skPoint(sketch, "E172.third.point", {"position": v(-1.12, 1.66) * mm});
            skCircle(sketch, "E173", {"center": v(0, 0) * mm, "radius": 2.5 * mm});
            skSolve(sketch);
        }
        {
            var Q0;
            Q0 = qSketchRegion(id + "F4", true);
            extrude(context, id + "F5", {"entities" : qUnion([Q0]), "operationType" : NewBodyOperationType.REMOVE, "oppositeDirection" : true, "depth" : 1.5 * mm, "offsetDistance" : 25 * mm});
        }
    });
